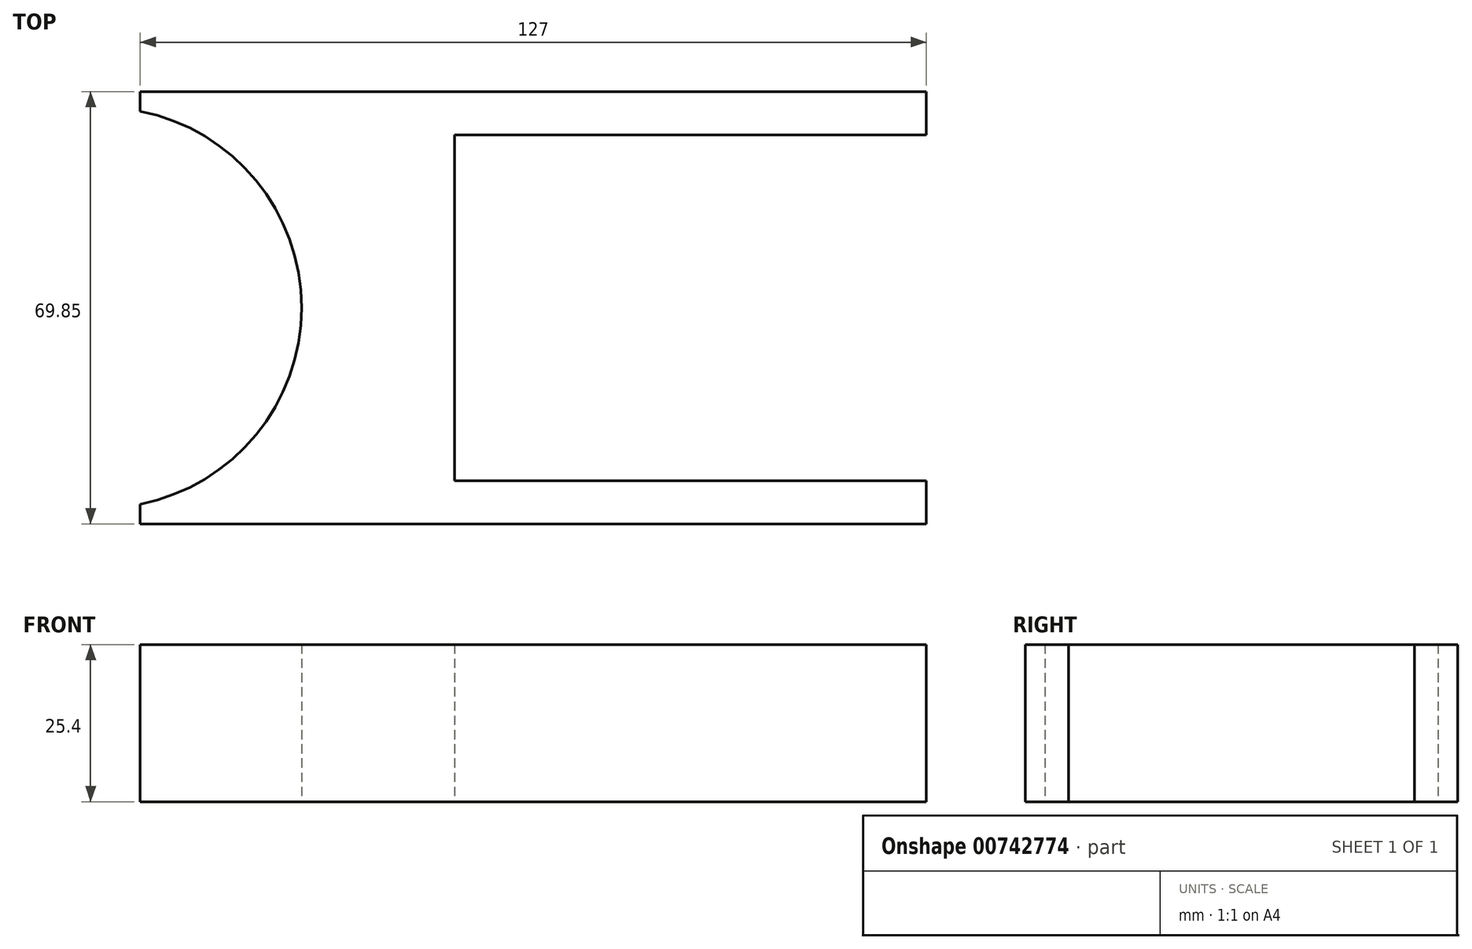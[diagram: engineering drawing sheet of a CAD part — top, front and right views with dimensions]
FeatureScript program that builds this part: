
annotation { "Feature Type Name" : "Feature", "Feature Type Description" : "" }
export const myFeature = defineFeature(function(context is Context, id is Id, definition is map)
    precondition{}
    {
        {
            var Q0;
            Q0=qCreatedBy(makeId("Top.planeOp"),FACE);
            var sketch = newSketch(context, id + "F0", { "sketchPlane" : qUnion([Q0])});
            skLineSegment(sketch, "E0.bottom", {"start": v(-62.41, 61.11) * mm, "end": v(64.59, 61.11) * mm});
            skLineSegment(sketch, "E0.top", {"start": v(-62.41, -8.74) * mm, "end": v(64.59, -8.74) * mm});
            skLineSegment(sketch, "E0.left", {"start": v(-62.41, 61.11) * mm, "end": v(-62.41, 57.94) * mm});
            skLineSegment(sketch, "E0.right", {"start": v(64.59, 61.11) * mm, "end": v(64.59, -8.74) * mm});
            skArc(sketch, "E1", {"start": v(-62.41, -5.56) * mm, "mid": v(-36.36, 26.19) * mm, "end": v(-62.41, 57.94) * mm});
            skLineSegment(sketch, "E2.trimOffspring", {"start": v(-62.41, -5.56) * mm, "end": v(-62.41, -8.74) * mm});
            skLineSegment(sketch, "E3.bottom", {"start": v(64.59, 54.13) * mm, "end": v(-11.61, 54.13) * mm});
            skLineSegment(sketch, "E3.top", {"start": v(64.59, -1.75) * mm, "end": v(-11.61, -1.75) * mm});
            skLineSegment(sketch, "E3.left", {"start": v(64.59, 54.13) * mm, "end": v(64.59, -1.75) * mm});
            skLineSegment(sketch, "E3.right", {"start": v(-11.61, 54.13) * mm, "end": v(-11.61, -1.75) * mm});
            skSolve(sketch);
        }
        {
            var Q0;
            {var subQ1=sQuery(id+"F0.wireOp",EDGE,"E0.bottom");Q0=makeQuery(id+"F0.imprint","IMPRINT",FACE,{"disambiguationData":[TD([[makeQuery(id+"F0.imprint","IMPRINT",EDGE,{"derivedFrom":subQ1}),-1.0]])]});}
            extrude(context, id + "F1", {"entities" : qUnion([Q0]), "depth" : 25.4 * mm, "offsetDistance" : 25.4 * mm});
        }
    });
